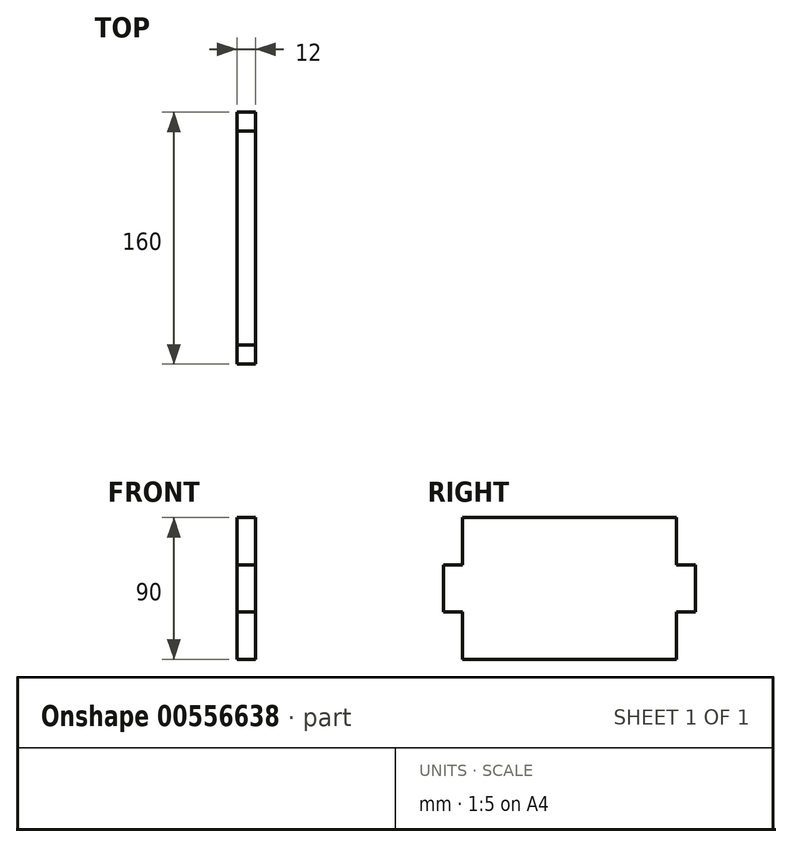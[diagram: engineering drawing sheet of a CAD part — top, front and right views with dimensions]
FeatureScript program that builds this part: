
annotation { "Feature Type Name" : "Feature", "Feature Type Description" : "" }
export const myFeature = defineFeature(function(context is Context, id is Id, definition is map)
    precondition{}
    {
        {
            var Q0;
            Q0=qCreatedBy(makeId("Right.planeOp"),FACE);
            var sketch = newSketch(context, id + "F0", { "sketchPlane" : qUnion([Q0])});
            skLineSegment(sketch, "E0", {"start": v(0, 0) * mm, "end": v(0, 30) * mm});
            skLineSegment(sketch, "E1", {"start": v(0, 30) * mm, "end": v(-12, 30) * mm});
            skLineSegment(sketch, "E2", {"start": v(-12, 30) * mm, "end": v(-12, 60) * mm});
            skLineSegment(sketch, "E3", {"start": v(-12, 60) * mm, "end": v(0, 60) * mm});
            skLineSegment(sketch, "E4", {"start": v(0, 60) * mm, "end": v(0, 90) * mm});
            skLineSegment(sketch, "E5", {"start": v(0, 90) * mm, "end": v(68, 90) * mm});
            skLineSegment(sketch, "E6", {"start": v(68, 90) * mm, "end": v(68, 0) * mm, "construction": true});
            skLineSegment(sketch, "E7", {"start": v(68, 0) * mm, "end": v(0, 0) * mm});
            skLineSegment(sketch, "E8.MirrorCS", {"start": v(136, 30) * mm, "end": v(148, 30) * mm});
            skLineSegment(sketch, "E9.MirrorCS", {"start": v(148, 30) * mm, "end": v(148, 60) * mm});
            skLineSegment(sketch, "E10.MirrorCS", {"start": v(136, 60) * mm, "end": v(136, 90) * mm});
            skLineSegment(sketch, "E11.MirrorCS", {"start": v(136, 0) * mm, "end": v(136, 30) * mm});
            skLineSegment(sketch, "E12.MirrorCS", {"start": v(136, 90) * mm, "end": v(68, 90) * mm});
            skLineSegment(sketch, "E13.MirrorCS", {"start": v(148, 60) * mm, "end": v(136, 60) * mm});
            skLineSegment(sketch, "E14.MirrorCS", {"start": v(68, 0) * mm, "end": v(136, 0) * mm});
            skSolve(sketch);
        }
        {
            var Q0;
            Q0 = qSketchRegion(id + "F0", true);
            extrude(context, id + "F1", {"entities" : qUnion([Q0]), "depth" : 12 * mm, "offsetDistance" : 25 * mm});
        }
    });
